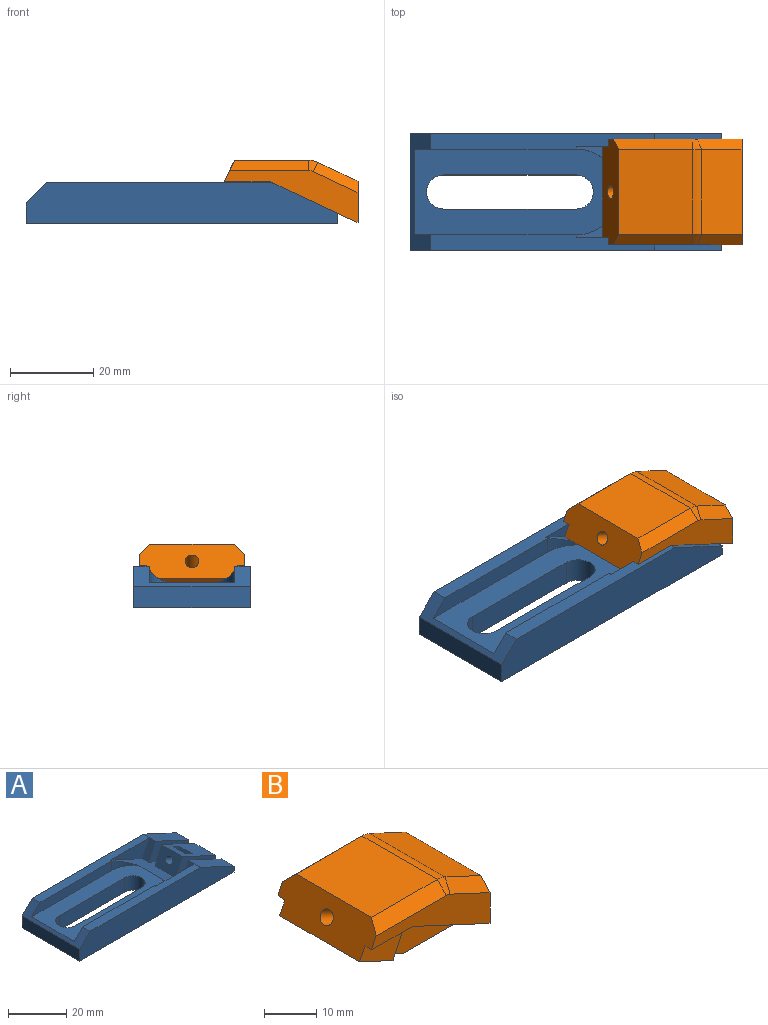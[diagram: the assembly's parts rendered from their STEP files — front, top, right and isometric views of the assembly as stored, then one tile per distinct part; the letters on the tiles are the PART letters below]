
ASSEMBLY  parts=2 mates=1
PART A: 40 faces, bbox 75.2x28x12.6 mm
  f0: plane 53.92x3.67mm, normal (0,0,1), area 185.1mm2, adj f6,f16,f19,f32,f36,f39
  f1: cylinder r=4.09mm len=8.19mm, axis (0,0,1), area 77.2mm2, adj f2,f4,f14,f38
  f2: plane 31.89x6mm, normal (0,1,0), area 191.4mm2, adj f1,f3,f14,f38
  f3: cylinder r=4.09mm len=8.19mm, axis (0,0,1), area 77.2mm2, adj f2,f4,f14,f38
  f4: plane 31.89x6mm, normal (0,-1,0), area 191.4mm2, adj f1,f3,f14,f38
  f5: plane 7.25x3.38mm, normal (-0.91,0,0.42), area 24mm2, adj f6,f16,f23,f32
  f6: plane 22x21.45mm, normal (0.42,0,0.91), area 246.6mm2, adj f0,f5,f12,f13,f14,f17,f21,f22
  f7: plane 16.08x10mm, normal (0.42,0,0.91), area 156.5mm2, adj f10,f12,f22,f24,f26,f27,f28,f29
  f8: cylinder r=1.65mm len=11.64mm, axis (-0.91,0,0.42), area 88.3mm2, adj f10,f14,f28
  f9: plane 6x2.5mm, normal (1,0,0), area 15mm2, adj f14,f16,f19,f23
  f10: plane 10x2.5mm, normal (1,0,0), area 24.3mm2, adj f7,f8,f14,f22,f24
  f11: plane 16.08x7.5mm, normal (0.42,0,0.91), area 106.5mm2, adj f13,f15,f17,f20,f21
  f12: plane 10x7.25mm, normal (-0.91,0,0.42), area 71.4mm2, adj f6,f7,f22,f24,f25
  f13: plane 7.25x3.38mm, normal (-0.91,0,0.42), area 24mm2, adj f6,f11,f21,f33
  f14: plane 75x28mm, normal (0,0,-1), area 1686.2mm2, adj f1,f2,f3,f4,f6,f8,f9,f10
  f15: plane 6x2.5mm, normal (1,0,0), area 15mm2, adj f11,f14,f20,f21
  f16: plane 16.08x7.5mm, normal (0.42,0,0.91), area 106.5mm2, adj f0,f5,f9,f19,f23
  f17: plane 53.92x3.67mm, normal (0,0,1), area 185.1mm2, adj f6,f11,f20,f33,f35,f39
  f18: plane 28x5mm, normal (-1,0,0), area 140mm2, adj f14,f19,f20,f39
  f19: plane 75x10mm, normal (0,-1,0), area 677.2mm2, adj f0,f9,f14,f16,f18,f39
  f20: plane 75x10mm, normal (0,1,0), area 677.2mm2, adj f11,f14,f15,f17,f18,f39
  f21: plane 19.46x10mm, normal (0,-1,0), area 114mm2, adj f6,f11,f13,f14,f15
  f22: plane 19.46x10mm, normal (0,1,0), area 114mm2, adj f6,f7,f10,f12,f14
  f23: plane 19.46x10mm, normal (0,1,0), area 114mm2, adj f5,f6,f9,f14,f16
  f24: plane 19.46x10mm, normal (0,-1,0), area 114mm2, adj f6,f7,f10,f12,f14
  f25: cylinder r=1.65mm len=5.02mm, axis (-0.91,0,0.42), area 41.5mm2, adj f12,f29
  f26: plane 6.2x5.38mm, normal (0,1,0), area 18.2mm2, adj f7,f28,f29,f30
  f27: plane 6.2x5.38mm, normal (0,-1,0), area 18.2mm2, adj f7,f28,f29,f31
  f28: plane 6.29x6mm, normal (-0.91,0,0.42), area 27.9mm2, adj f7,f8,f26,f27,f30,f31
  f29: plane 6.29x6mm, normal (0.91,0,-0.42), area 27.9mm2, adj f7,f25,f26,f27,f30,f31
  f30: plane 3.9x3.05mm, normal (0.37,0.5,0.78), area 12.1mm2, adj f26,f28,f29,f31
  f31: plane 3.9x3.05mm, normal (0.37,-0.5,0.78), area 12.1mm2, adj f27,f28,f29,f30
  f32: plane 18.93x7.25mm, normal (0,1,0), area 68.6mm2, adj f0,f5,f6
  f33: plane 18.93x7.25mm, normal (0,-1,0), area 68.6mm2, adj f6,f13,f17
  f34: cylinder r=10.33mm len=8.58mm, axis (0,0,1), area 18.5mm2, adj f6,f36,f38
  f35: plane 38.99x4mm, normal (0,-1,0), area 147.9mm2, adj f17,f37,f38,f39
  f36: plane 38.99x4mm, normal (0,1,0), area 147.9mm2, adj f0,f34,f38,f39
  f37: cylinder r=10.33mm len=8.58mm, axis (0,0,1), area 18.5mm2, adj f6,f35,f38
  f38: plane 47.56x20.66mm, normal (0,0,1), area 645.8mm2, adj f1,f2,f3,f4,f6,f34,f35,f36
  f39: plane 28x5mm, normal (-0.71,0,0.71), area 81.1mm2, adj f0,f17,f18,f19,f20,f35,f36,f38
PART B: 31 faces, bbox 33.5x25.4x15.2 mm
  f0: plane 25.4x8.19mm, normal (-0.91,0,0.42), area 201.8mm2, adj f1,f7,f8,f13,f15,f16,f17,f22
  f1: plane 21.7x14.96mm, normal (-0.42,0,-0.91), area 252.1mm2, adj f0,f3,f5,f6,f9,f10,f18,f19
  f2: plane 2.7x2.5mm, normal (1,0,0), area 6.7mm2, adj f3,f11,f20,f21
  f3: plane 13.57x2.7mm, normal (0,0,-1), area 36.6mm2, adj f1,f2,f20,f21
  f4: plane 2.7x2.5mm, normal (1,0,0), area 6.7mm2, adj f5,f11,f18,f19
  f5: plane 13.57x2.7mm, normal (0,0,-1), area 36.6mm2, adj f1,f4,f18,f19
  f6: plane 7.25x3.38mm, normal (0.91,0,-0.42), area 24mm2, adj f1,f11,f21,f23
  f7: plane 32.12x12.5mm, normal (0,-1,0), area 158mm2, adj f0,f11,f14,f17,f28,f29,f30
  f8: plane 32.12x12.5mm, normal (0,1,0), area 158mm2, adj f0,f11,f14,f16,f25,f26,f27
  f9: plane 7.25x3.38mm, normal (0.91,0,-0.42), area 24mm2, adj f1,f11,f19,f22
  f10: plane 10.3x7.25mm, normal (0.91,0,-0.42), area 73.8mm2, adj f1,f11,f15,f18,f20
  f11: plane 25.4x21.08mm, normal (-0.42,0,-0.91), area 495.1mm2, adj f2,f4,f6,f7,f8,f9,f10,f14
  f12: plane 20.4x9.72mm, normal (0.42,0,0.91), area 218.7mm2, adj f14,f24,f27,f30
  f13: plane 20.4x17.88mm, normal (0,0,1), area 364.7mm2, adj f0,f24,f25,f28
  f14: plane 25.4x10mm, normal (1,0,0), area 247.1mm2, adj f7,f8,f11,f12,f27,f30
  f15: cylinder r=1.65mm len=10.46mm, axis (-0.91,0,0.42), area 103.7mm2, adj f0,f10
  f16: plane 11.03x1.85mm, normal (0,0,-1), area 20.4mm2, adj f0,f8,f11,f22
  f17: plane 11.03x1.85mm, normal (0,0,-1), area 20.4mm2, adj f0,f7,f11,f23
  f18: plane 19.46x10mm, normal (0,-1,0), area 114mm2, adj f1,f4,f5,f10,f11
  f19: plane 19.46x10mm, normal (0,1,0), area 114mm2, adj f1,f4,f5,f9,f11
  f20: plane 19.46x10mm, normal (0,1,0), area 114mm2, adj f1,f2,f3,f10,f11
  f21: plane 19.46x10mm, normal (0,-1,0), area 114mm2, adj f1,f2,f3,f6,f11
  f22: plane 12.44x7.25mm, normal (0,1,0), area 56.7mm2, adj f0,f1,f9,f16
  f23: plane 12.44x7.25mm, normal (0,-1,0), area 56.7mm2, adj f0,f1,f6,f17
  f24: cylinder r=5mm len=20.4mm, axis (0,1,0), area 44.5mm2, adj f12,f13,f26,f29
  f25: plane 19.04x2.5mm, normal (0,0.71,0.71), area 65.3mm2, adj f0,f8,f13,f26
  f26: cone r=2.5mm half-angle=45deg, axis (0,-1,0), area 5.8mm2, adj f8,f24,f25,f27
  f27: plane 10.77x7.29mm, normal (0.3,0.71,0.64), area 40mm2, adj f8,f12,f14,f26
  f28: plane 19.04x2.5mm, normal (0,-0.71,0.71), area 65.3mm2, adj f0,f7,f13,f29
  f29: cone r=2.5mm half-angle=45deg, axis (0,1,0), area 5.8mm2, adj f7,f24,f28,f30
  f30: plane 10.77x7.29mm, normal (0.3,-0.71,0.64), area 40mm2, adj f7,f12,f14,f29
PLACE A t=(-8.19,0,-2.89)mm fixed
PLACE B t=(-8.32,0,-2.83)mm
MATE planar A.f6 <-> B.f1  axis (0.42,0,0.91) through (-31.1,0,1.46)mm
